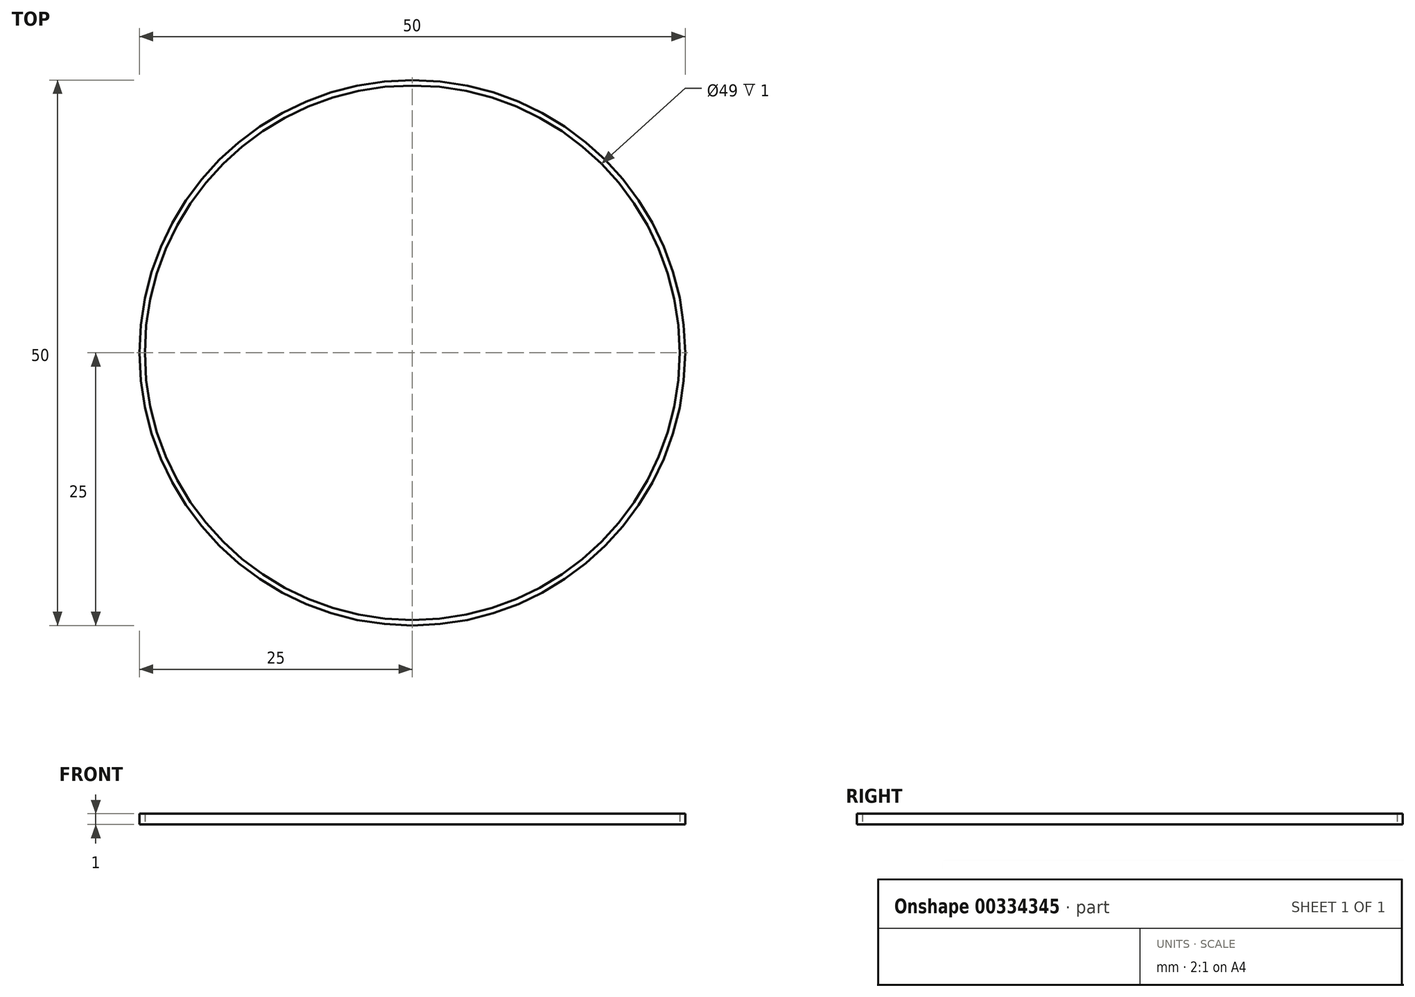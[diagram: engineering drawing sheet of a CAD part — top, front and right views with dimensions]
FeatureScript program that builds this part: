
annotation { "Feature Type Name" : "Feature", "Feature Type Description" : "" }
export const myFeature = defineFeature(function(context is Context, id is Id, definition is map)
    precondition{}
    {
        {
            var Q0;
            Q0=qCreatedBy(makeId("Top.planeOp"),FACE);
            var sketch = newSketch(context, id + "F0", { "sketchPlane" : qUnion([Q0])});
            skCircle(sketch, "E0", {"center": v(0, 0) * mm, "radius": 25 * mm});
            skCircle(sketch, "E1", {"center": v(0, 0) * mm, "radius": 24.5 * mm});
            skSolve(sketch);
        }
        {
            var Q0;
            Q0 = qSketchRegion(id + "F0", true);
            extrude(context, id + "F1", {"entities" : qUnion([Q0]), "depth" : 1 * mm});
        }
    });
